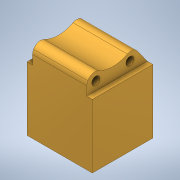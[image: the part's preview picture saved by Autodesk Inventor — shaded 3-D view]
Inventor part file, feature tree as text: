
AUTODESK INVENTOR PART (.ipt)
format: ipt  version: 2020 (Build 240168000, 168)  size: 190,976 bytes
history: native  units: in
note: dims shown in document units (in); Inventor stores cm internally (conversion verified against a paired STEP export)
features: extrude x5, sketch x5, projected_geometry x4, fillet x1
ambient origin geometry x8: Origin, YZ Plane, XZ Plane, XY Plane, X Axis, Y Axis, Z Axis, Center Point
bodies: Solid1 (feature_tree)
feature tree (15):
  extrude  "Extrusion1"  Depth=0.4523in
  extrude  "Extrusion4"  Depth=0.8586in
  extrude  "Extrusion5"  Depth=1.378in TaperAngle=0.0deg
  extrude  "Extrusion6"  Depth=0.8658in
  extrude  "Extrusion7"  Depth=1.378in TaperAngle=0.0deg
  fillet  "Fillet1"  Radius=1.5354in
  sketch  "Sketch1"  dims[d0=0.2087in d1=0.2087in d3=0.4523in]
  sketch  "Sketch4"  dims[d4=0.2118in d5=0.8586in]
  sketch  "Sketch6"  dims[d6=0.8656in d7=1.378in d8=0.0in]
  projected_geometry  "Projected Loop3"
  sketch  "Sketch7"  dims[d22=0.8658in d23=0.8658in]
  projected_geometry  "Projected Loop4"
  projected_geometry  "Projected Loop5"
  sketch  "Sketch8"  dims[d24=0.2087in d25=1.378in d26=0.0in d32=1.5354in d33=1.6535in d34=0.0in d35=1.622in d37=1.6535in d38=0.0in d39=0.7874in d40=0.3937in d41=0.0in d42=0.1969in]
  projected_geometry  "Projected Loop6"
